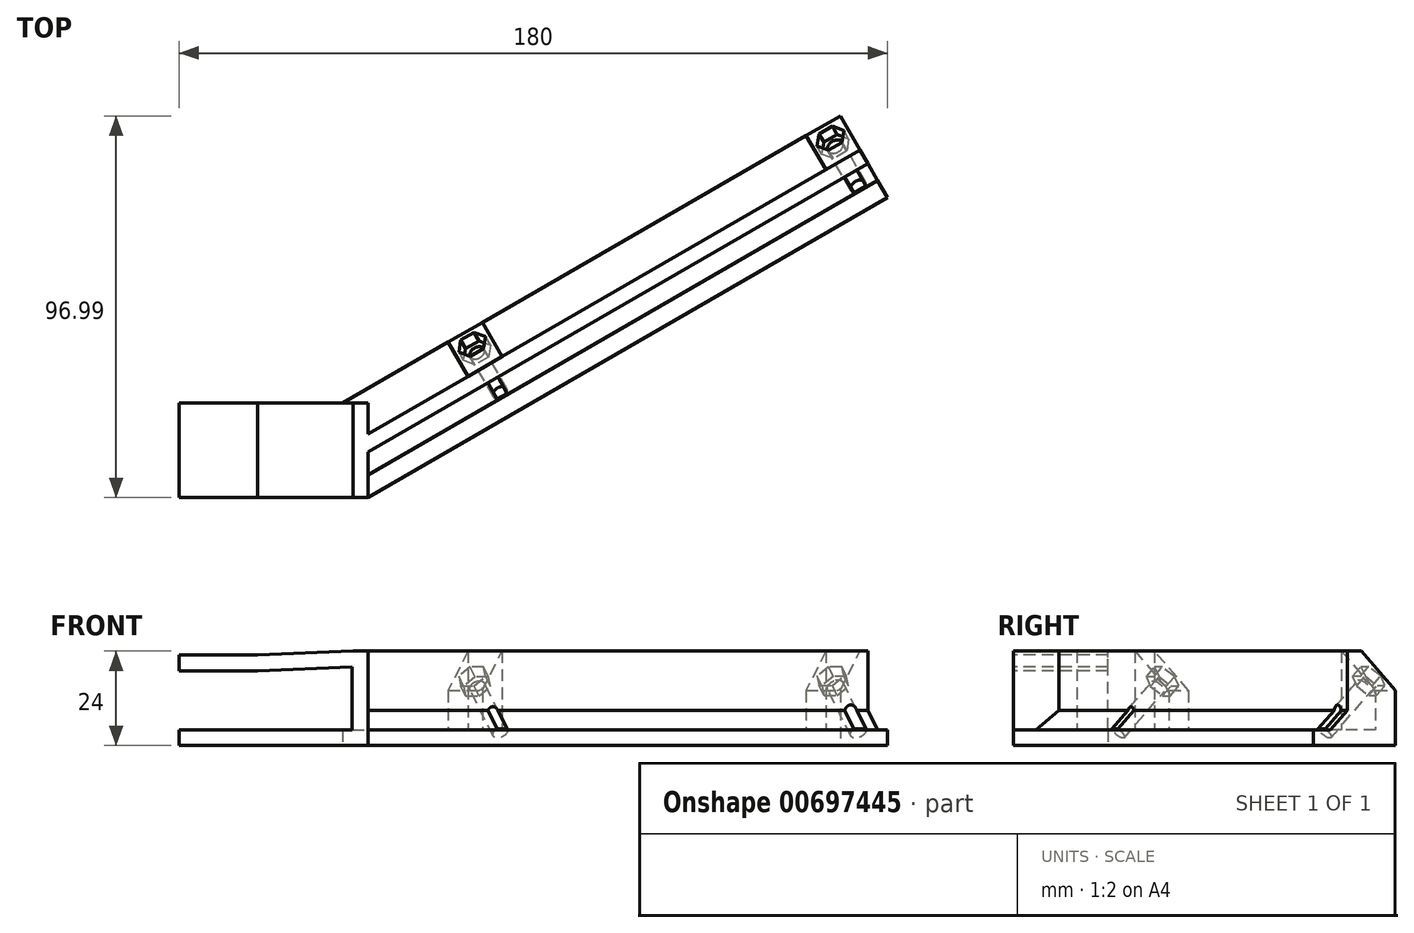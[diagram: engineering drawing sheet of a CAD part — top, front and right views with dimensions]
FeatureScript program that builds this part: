
annotation { "Feature Type Name" : "Feature", "Feature Type Description" : "" }
export const myFeature = defineFeature(function(context is Context, id is Id, definition is map)
    precondition{}
    {
        {
            var Q0;
            Q0=qCreatedBy(makeId("Top.planeOp"),FACE);
            var sketch = newSketch(context, id + "F0", { "sketchPlane" : qUnion([Q0])});
            skLineSegment(sketch, "E0.bottom", {"start": v(-77.3, 8.76) * mm, "end": v(-29.3, 8.76) * mm});
            skLineSegment(sketch, "E0.top", {"start": v(-77.3, -15.24) * mm, "end": v(-29.3, -15.24) * mm});
            skLineSegment(sketch, "E0.left", {"start": v(-77.3, 8.76) * mm, "end": v(-77.3, -15.24) * mm});
            skLineSegment(sketch, "E0.right", {"start": v(-29.3, 8.76) * mm, "end": v(-29.3, -15.24) * mm});
            skLineSegment(sketch, "E1", {"start": v(-29.3, -15.24) * mm, "end": v(102.7, 60.97) * mm});
            skLineSegment(sketch, "E2", {"start": v(102.7, 60.97) * mm, "end": v(90.7, 81.75) * mm});
            skLineSegment(sketch, "E3", {"start": v(90.7, 81.75) * mm, "end": v(-35.73, 8.76) * mm});
            skLineSegment(sketch, "E4", {"start": v(-35.73, 8.76) * mm, "end": v(-23.73, -12.03) * mm});
            skSolve(sketch);
        }
        {
            var Q0;
            Q0=qSketchRegion(id+"F0",true);
            extrude(context, id + "F1", {"entities" : qUnion([Q0]), "depth" : 4 * mm, "offsetDistance" : 25 * mm});
        }
        {
            var Q0;
            Q0=makeQuery(id+"F1.opExtrude","SWEPT_FACE",FACE,{"disambiguationData":[OSD([sQuery(id+"F0.wireOp",EDGE,"E0.top")])]});
            var sketch = newSketch(context, id + "F2", { "sketchPlane" : qUnion([Q0])});
            skLineSegment(sketch, "E5.bottom", {"start": v(-29.3, 4) * mm, "end": v(-33.3, 4) * mm});
            skLineSegment(sketch, "E5.top", {"start": v(-29.3, 20) * mm, "end": v(-33.3, 20) * mm});
            skLineSegment(sketch, "E5.left", {"start": v(-29.3, 4) * mm, "end": v(-29.3, 20) * mm});
            skLineSegment(sketch, "E5.right", {"start": v(-33.3, 4) * mm, "end": v(-33.3, 20) * mm});
            skLineSegment(sketch, "E6", {"start": v(-77.3, 4) * mm, "end": v(-77.3, 19) * mm, "construction": true});
            skLineSegment(sketch, "E7", {"start": v(-57.3, 4) * mm, "end": v(-57.3, 19) * mm, "construction": true});
            skLineSegment(sketch, "E8.bottom", {"start": v(-77.3, 19) * mm, "end": v(-57.3, 19) * mm});
            skLineSegment(sketch, "E8.top", {"start": v(-77.3, 23) * mm, "end": v(-57.3, 23) * mm});
            skLineSegment(sketch, "E8.left", {"start": v(-77.3, 19) * mm, "end": v(-77.3, 23) * mm});
            skLineSegment(sketch, "E8.right", {"start": v(-57.3, 19) * mm, "end": v(-57.3, 23) * mm});
            skLineSegment(sketch, "E9", {"start": v(-29.3, 24) * mm, "end": v(-29.3, 20) * mm});
            skLineSegment(sketch, "E10", {"start": v(-29.3, 24) * mm, "end": v(-33.13, 24) * mm});
            skLineSegment(sketch, "E11", {"start": v(-57.3, 23) * mm, "end": v(-33.13, 24) * mm});
            skPoint(sketch, "E12.orphan", {"position": v(-36.96, 24) * mm});
            skLineSegment(sketch, "E13", {"start": v(-57.3, 19) * mm, "end": v(-33.3, 20) * mm});
            skSolve(sketch);
        }
        {
            var Q0;
            Q0=qSketchRegion(id+"F2",true);
            extrude(context, id + "F3", {"entities" : qUnion([Q0]), "operationType" : NewBodyOperationType.ADD, "oppositeDirection" : true, "depth" : 24 * mm, "offsetDistance" : 25 * mm});
        }
        {
            var Q0;
            Q0=makeQuery(id+"F1.opExtrude","CAP_FACE",FACE,{"disambiguationData":[OSD([sQuery(id+"F0.wireOp",EDGE,"E0.bottom"),sQuery(id+"F0.wireOp",EDGE,"E0.top"),sQuery(id+"F0.wireOp",EDGE,"E0.left"),sQuery(id+"F0.wireOp",EDGE,"E1"),sQuery(id+"F0.wireOp",EDGE,"E2"),sQuery(id+"F0.wireOp",EDGE,"E3")])],"isStart":false});
            var sketch = newSketch(context, id + "F4", { "sketchPlane" : qUnion([Q0])});
            skLineSegment(sketch, "E14", {"start": v(97.7, 69.63) * mm, "end": v(95.7, 73.1) * mm});
            skLineSegment(sketch, "E15", {"start": v(95.7, 73.1) * mm, "end": v(-29.3, 0.92) * mm});
            skLineSegment(sketch, "E16", {"start": v(97.7, 69.63) * mm, "end": v(-29.3, -3.7) * mm});
            skLineSegment(sketch, "E17", {"start": v(-29.3, -3.7) * mm, "end": v(-29.3, 0.92) * mm});
            skSolve(sketch);
        }
        {
            var Q0;
            Q0=qSketchRegion(id+"F4",true);
            extrude(context, id + "F5", {"entities" : qUnion([Q0]), "operationType" : NewBodyOperationType.ADD, "depth" : 20 * mm, "offsetDistance" : 25 * mm});
        }
        {
            var Q0;
            {var subQ10=sQuery(id+"F0.wireOp",EDGE,"E3");var subQ11=sQuery(id+"F0.wireOp",EDGE,"E0.bottom");var subQ12=sQuery(id+"F0.wireOp",EDGE,"E2");var subQ13=sQuery(id+"F0.wireOp",EDGE,"E0.top");var subQ14=sQuery(id+"F0.wireOp",EDGE,"E0.left");Q0=makeQuery(id+"F5.boolean.opBoolean","SPLIT",FACE,{"disambiguationData":[TD([makeQuery(id+"F1.opExtrude","SWEPT_FACE",FACE,{"disambiguationData":[OSD([subQ11])]})])],"derivedFrom":makeQuery(id+"F1.opExtrude","CAP_FACE",FACE,{"disambiguationData":[OSD([subQ11,subQ13,subQ14,sQuery(id+"F0.wireOp",EDGE,"E1"),subQ12,subQ10])],"isStart":false})});}
            var sketch = newSketch(context, id + "F6", { "sketchPlane" : qUnion([Q0])});
            skLineSegment(sketch, "E18", {"start": v(95.7, 73.1) * mm, "end": v(90.7, 81.75) * mm});
            skLineSegment(sketch, "E19", {"start": v(90.7, 81.75) * mm, "end": v(82.04, 76.75) * mm});
            skLineSegment(sketch, "E20", {"start": v(82.04, 76.75) * mm, "end": v(87.04, 68.1) * mm});
            skLineSegment(sketch, "E21", {"start": v(87.04, 68.1) * mm, "end": v(95.7, 73.1) * mm});
            skLineSegment(sketch, "E22", {"start": v(-0.24, 29.25) * mm, "end": v(4.76, 20.6) * mm});
            skLineSegment(sketch, "E23", {"start": v(4.76, 20.6) * mm, "end": v(-3.9, 15.6) * mm});
            skLineSegment(sketch, "E24", {"start": v(-3.9, 15.6) * mm, "end": v(-8.9, 24.25) * mm});
            skLineSegment(sketch, "E25", {"start": v(-8.9, 24.25) * mm, "end": v(-0.24, 29.25) * mm});
            skSolve(sketch);
        }
        {
            var Q0;
            Q0=qSketchRegion(id+"F6",true);
            extrude(context, id + "F7", {"entities" : qUnion([Q0]), "operationType" : NewBodyOperationType.ADD, "depth" : 20 * mm, "offsetDistance" : 25 * mm});
        }
        {
            var Q0;
            Q0=makeQuery(id+"F7.opExtrude","CAP_EDGE",EDGE,{"disambiguationData":[OSD([sQuery(id+"F6.wireOp",EDGE,"E19")])],"isStart":false});
            var Q1;
            Q1=makeQuery(id+"F7.opExtrude","CAP_EDGE",EDGE,{"disambiguationData":[OSD([sQuery(id+"F6.wireOp",EDGE,"E25")])],"isStart":false});
            chamfer(context, id + "F8", {"entities" : qUnion([Q0, Q1]), "width" : 10 * mm, "tangentPropagation" : true});
        }
        {
            var Q0;
            Q0=makeQuery(id+"F5.opExtrude","CAP_EDGE",EDGE,{"disambiguationData":[OSD([sQuery(id+"F4.wireOp",EDGE,"E16")])],"isStart":true});
            var Q1;
            {var subQ0=sQuery(id+"F4.wireOp",EDGE,"E15");Q1=makeQuery(id+"F7.boolean.opBoolean","SPLIT",EDGE,{"disambiguationData":[TD([makeQuery(id+"F7.opExtrude","SWEPT_FACE",FACE,{"disambiguationData":[OSD([sQuery(id+"F6.wireOp",EDGE,"E20")])]})])],"derivedFrom":makeQuery(id+"F5.opExtrude","CAP_EDGE",EDGE,{"disambiguationData":[OSD([subQ0])],"isStart":true})});}
            chamfer(context, id + "F9", {"entities" : qUnion([Q0, Q1]), "width" : 5 * mm, "tangentPropagation" : true});
        }
        {
            var Q0;
            Q0=makeQuery(id+"F8.opChamfer","BLEND_FACE",FACE,{"disambiguationData":[OSD([sQuery(id+"F6.wireOp",EDGE,"E25")])]});
            var sketch = newSketch(context, id + "F10", { "sketchPlane" : qUnion([Q0])});
            skCircle(sketch, "E26", {"center": v(7.55, 6.43) * mm, "radius": 2 * mm});
            skCircle(sketch, "E27", {"center": v(104.82, 45.97) * mm, "radius": 2.16 * mm});
            skSolve(sketch);
        }
        {
            var Q0;
            Q0=qSketchRegion(id+"F10",true);
            extrude(context, id + "F11", {"entities" : qUnion([Q0]), "operationType" : NewBodyOperationType.REMOVE, "oppositeDirection" : true, "depth" : 20.1 * mm, "offsetDistance" : 25 * mm});
        }
        {
            var Q0;
            Q0=makeQuery(id+"F8.opChamfer","BLEND_FACE",FACE,{"disambiguationData":[OSD([sQuery(id+"F6.wireOp",EDGE,"E19")])]});
            var sketch = newSketch(context, id + "F12", { "sketchPlane" : qUnion([Q0])});
            skCircle(sketch, "E28.cCircle", {"center": v(104.82, 45.97) * mm, "radius": 3.4 * mm, "construction": true});
            skLineSegment(sketch, "E28.0", {"start": v(104.3, 42.08) * mm, "end": v(101.19, 44.48) * mm});
            skLineSegment(sketch, "E28.1", {"start": v(101.19, 44.48) * mm, "end": v(101.72, 48.37) * mm});
            skLineSegment(sketch, "E28.2", {"start": v(101.72, 48.37) * mm, "end": v(105.35, 49.86) * mm});
            skLineSegment(sketch, "E28.3", {"start": v(105.35, 49.86) * mm, "end": v(108.46, 47.45) * mm});
            skLineSegment(sketch, "E28.4", {"start": v(108.46, 47.45) * mm, "end": v(107.92, 43.56) * mm});
            skLineSegment(sketch, "E28.5", {"start": v(107.92, 43.56) * mm, "end": v(104.3, 42.08) * mm});
            skPoint(sketch, "E28.0.midPoint", {"position": v(102.74, 43.28) * mm});
            skSolve(sketch);
        }
        {
            var Q0;
            Q0=qSketchRegion(id+"F12",true);
            extrude(context, id + "F13", {"entities" : qUnion([Q0]), "operationType" : NewBodyOperationType.REMOVE, "oppositeDirection" : true, "depth" : 3.5 * mm, "offsetDistance" : 25 * mm});
        }
        {
            var Q0;
            Q0=makeQuery(id+"F8.opChamfer","BLEND_FACE",FACE,{"disambiguationData":[OSD([sQuery(id+"F6.wireOp",EDGE,"E25")])]});
            var sketch = newSketch(context, id + "F14", { "sketchPlane" : qUnion([Q0])});
            skCircle(sketch, "E29.cCircle", {"center": v(7.55, 6.43) * mm, "radius": 3.4 * mm, "construction": true});
            skLineSegment(sketch, "E29.0", {"start": v(7.02, 2.54) * mm, "end": v(3.92, 4.94) * mm});
            skLineSegment(sketch, "E29.1", {"start": v(3.92, 4.94) * mm, "end": v(4.45, 8.83) * mm});
            skLineSegment(sketch, "E29.2", {"start": v(4.45, 8.83) * mm, "end": v(8.08, 10.32) * mm});
            skLineSegment(sketch, "E29.3", {"start": v(8.08, 10.32) * mm, "end": v(11.19, 7.91) * mm});
            skLineSegment(sketch, "E29.4", {"start": v(11.19, 7.91) * mm, "end": v(10.65, 4.02) * mm});
            skLineSegment(sketch, "E29.5", {"start": v(10.65, 4.02) * mm, "end": v(7.02, 2.54) * mm});
            skPoint(sketch, "E29.0.midPoint", {"position": v(5.47, 3.74) * mm});
            skSolve(sketch);
        }
        {
            var Q0;
            Q0=qSketchRegion(id+"F14",true);
            extrude(context, id + "F15", {"entities" : qUnion([Q0]), "operationType" : NewBodyOperationType.REMOVE, "oppositeDirection" : true, "depth" : 3.5 * mm, "offsetDistance" : 25 * mm});
        }
    });
